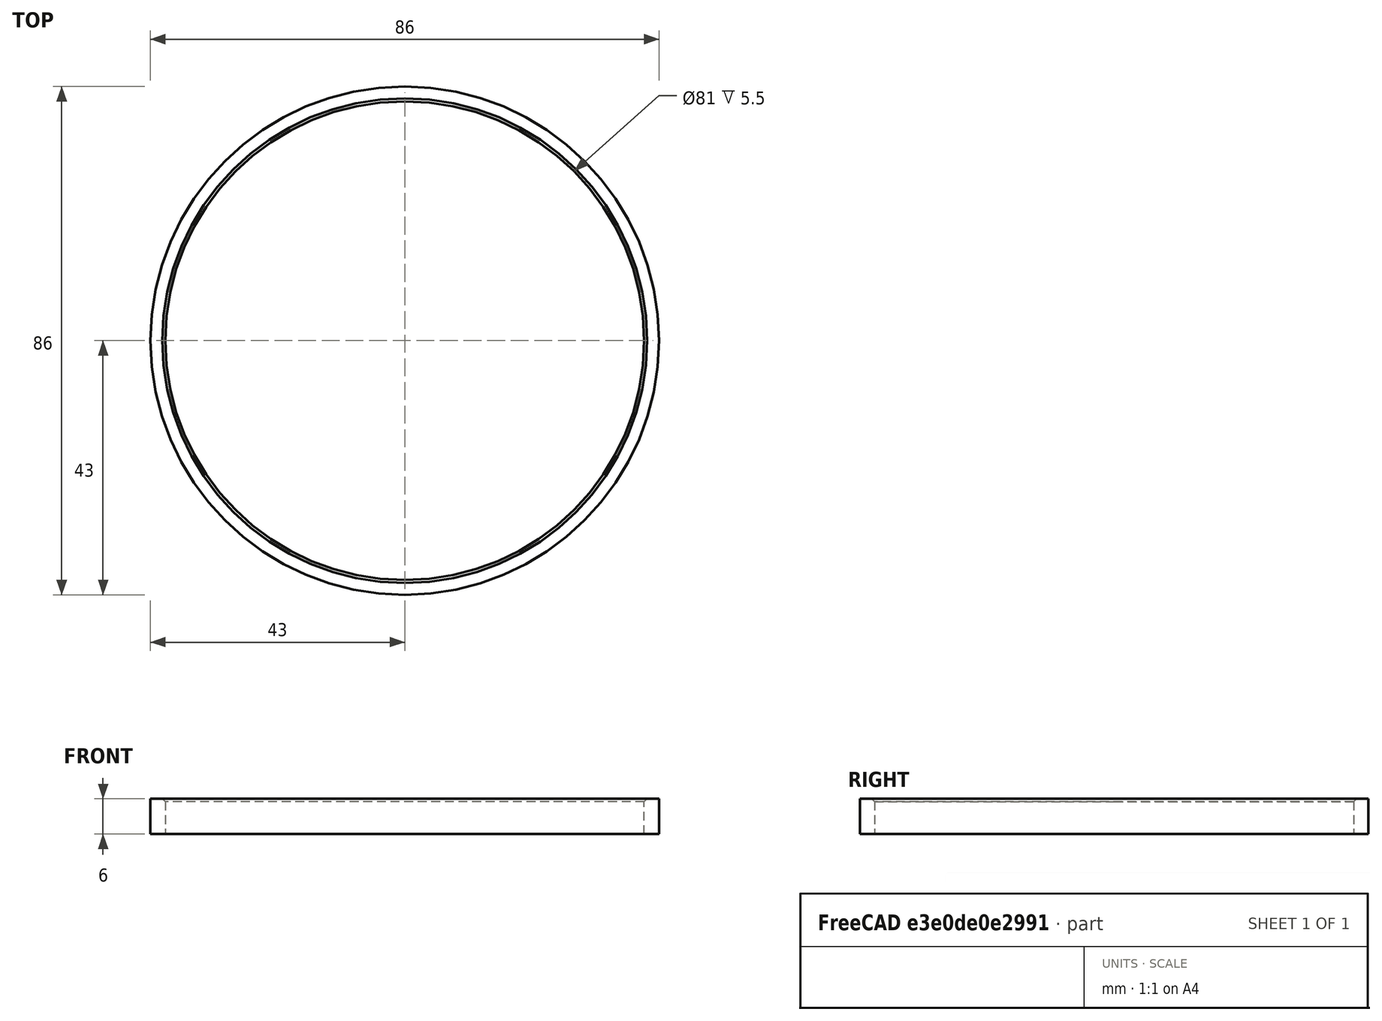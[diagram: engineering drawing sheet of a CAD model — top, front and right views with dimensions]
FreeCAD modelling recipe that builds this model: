
FCSTD DOCUMENT  (FreeCAD 0.19R24276 (Git))
Label: BLDC_GT2_part_3_Ring_d81_d86
License: All rights reserved
LicenseURL: http://en.wikipedia.org/wiki/All_rights_reserved
objects: Sketcher::SketchObject×1, PartDesign::Pad×1, PartDesign::Chamfer×1, PartDesign::Body×1
note: 6 computed .brp shape members not serialized (recipe doc carries the construction recipe); baked Part::Feature solids carry a one-line shape summary decoded from their .brp

FEATURE [Sketcher::SketchObject] Sketch
  FullyConstrained = true
  MapMode = 5
  Support = -> [XY_Plane]
  sketch-geometry (2):
    g0: Circle CenterX=0 CenterY=0 CenterZ=0 NormalX=0 NormalY=0 NormalZ=1 AngleXU=0 Radius=40.5
    g1: Circle CenterX=0 CenterY=0 CenterZ=0 NormalX=0 NormalY=0 NormalZ=1 AngleXU=0 Radius=43
  constraints (4):
    c: Coincident(g0,g-1)
    c: Coincident(g1,g0)
    c: Diameter(g0) = 81
    c: Diameter(g1) = 86
FEATURE [PartDesign::Pad] Pad
  Direction = (1,1,1)
  Length = 6
  Length2 = 100
  Profile = -> Sketch
  Type = 0
FEATURE [PartDesign::Chamfer] Chamfer
  Angle = 45
  Base = -> Pad [Edge6]
  BaseFeature = -> Pad
  ChamferType = 0
  FlipDirection = false
  Size = 0.5
  Size2 = 1
  SupportTransform = false
FEATURE [PartDesign::Body] Body
  Group = -> [Sketch,Pad,Chamfer]
  Origin = -> Origin
  Tip = -> Chamfer
